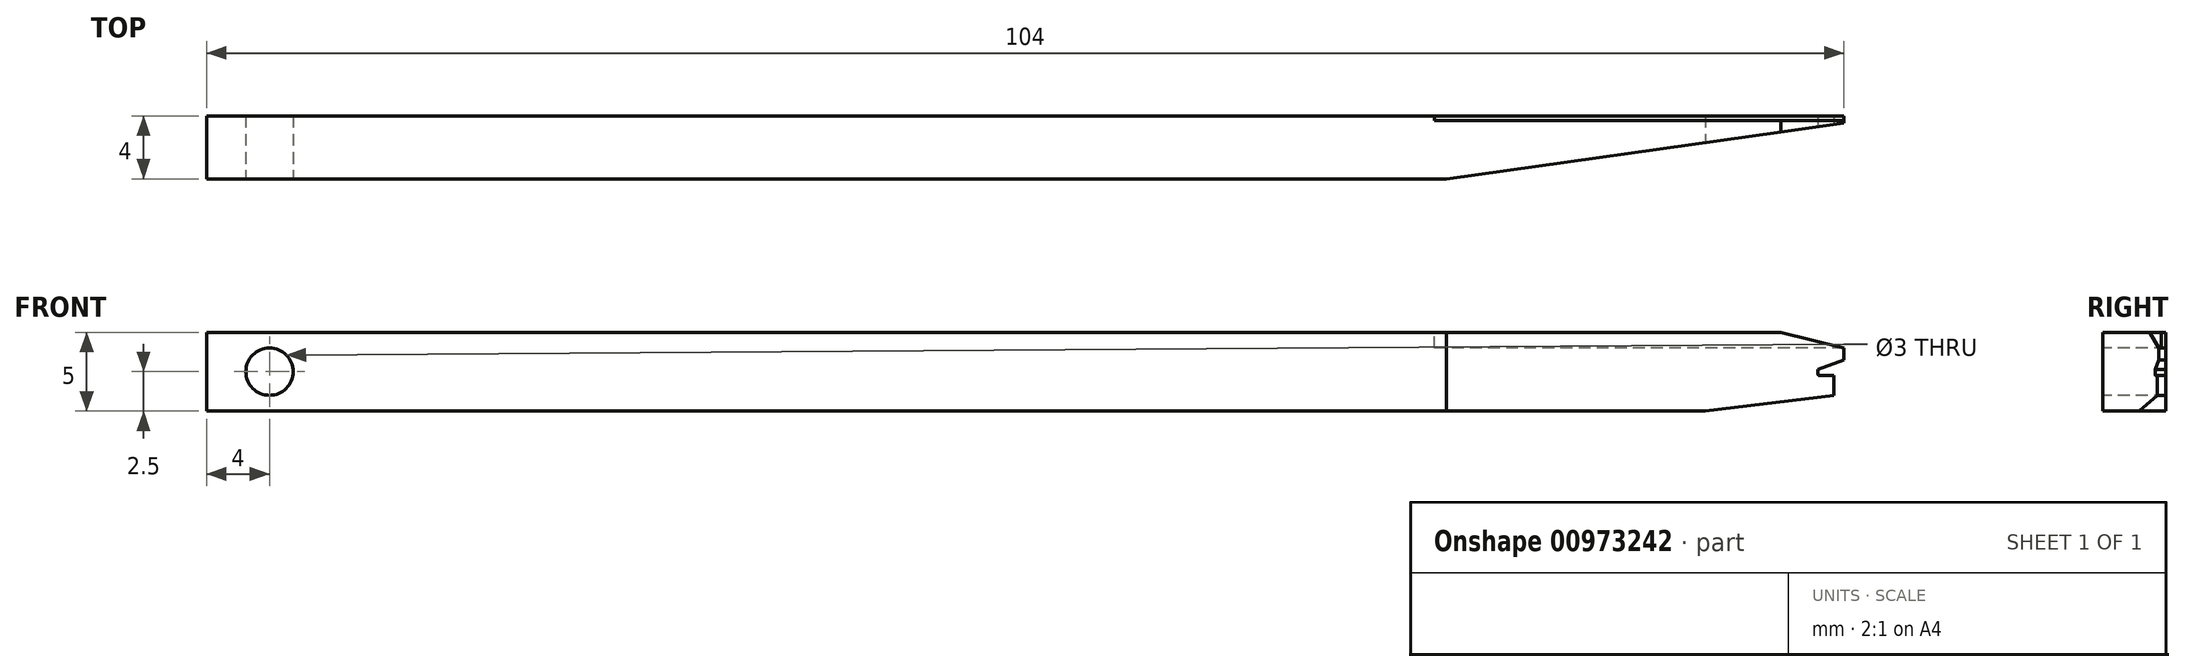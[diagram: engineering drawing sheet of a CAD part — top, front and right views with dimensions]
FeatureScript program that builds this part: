
annotation { "Feature Type Name" : "Feature", "Feature Type Description" : "" }
export const myFeature = defineFeature(function(context is Context, id is Id, definition is map)
    precondition{}
    {
        {
            var Q0;
            Q0=qCreatedBy(makeId("Front.planeOp"),FACE);
            var sketch = newSketch(context, id + "F0", { "sketchPlane" : qUnion([Q0])});
            skLineSegment(sketch, "E0.bottom", {"start": v(52, -2.5) * mm, "end": v(-52, -2.5) * mm});
            skLineSegment(sketch, "E0.top", {"start": v(52, 2.5) * mm, "end": v(-52, 2.5) * mm});
            skLineSegment(sketch, "E0.left", {"start": v(52, -2.5) * mm, "end": v(52, 2.5) * mm});
            skLineSegment(sketch, "E0.right", {"start": v(-52, -2.5) * mm, "end": v(-52, 2.5) * mm});
            skPoint(sketch, "E0.middle", {"position": v(0, 0) * mm});
            skSolve(sketch);
        }
        {
            var Q0;
            Q0 = qSketchRegion(id + "F0", true);
            extrude(context, id + "F1", {"entities" : qUnion([Q0]), "depth" : 4 * mm, "offsetDistance" : 25 * mm});
        }
        {
            var Q0;
            Q0=makeQuery(id+"F1.opExtrude","CAP_FACE",FACE,{"disambiguationData":[OSD([sQuery(id+"F0.wireOp",EDGE,"E0.bottom"),sQuery(id+"F0.wireOp",EDGE,"E0.top"),sQuery(id+"F0.wireOp",EDGE,"E0.left"),sQuery(id+"F0.wireOp",EDGE,"E0.right")])],"isStart":false});
            var sketch = newSketch(context, id + "F2", { "sketchPlane" : qUnion([Q0])});
            skLineSegment(sketch, "E1", {"start": v(-52, -2.5) * mm, "end": v(-48, -2.5) * mm});
            skLineSegment(sketch, "E2", {"start": v(-48, -2.5) * mm, "end": v(-48, 0) * mm});
            skCircle(sketch, "E3", {"center": v(-48, 0) * mm, "radius": 1.5 * mm});
            skSolve(sketch);
        }
        {
            var Q0;
            Q0 = qSketchRegion(id + "F2", true);
            extrude(context, id + "F3", {"entities" : qUnion([Q0]), "operationType" : NewBodyOperationType.REMOVE, "endBound" : BoundingType.UP_TO_NEXT, "oppositeDirection" : true, "depth" : 25 * mm, "offsetDistance" : 25 * mm});
        }
        {
            var Q0;
            Q0=makeQuery(id+"F1.opExtrude","CAP_FACE",FACE,{"disambiguationData":[OSD([sQuery(id+"F0.wireOp",EDGE,"E0.bottom"),sQuery(id+"F0.wireOp",EDGE,"E0.top"),sQuery(id+"F0.wireOp",EDGE,"E0.left"),sQuery(id+"F0.wireOp",EDGE,"E0.right")])],"isStart":false});
            var sketch = newSketch(context, id + "F4", { "sketchPlane" : qUnion([Q0])});
            skLineSegment(sketch, "E4.bottom", {"start": v(52, -2.5) * mm, "end": v(51.35, -2.5) * mm});
            skLineSegment(sketch, "E4.top", {"start": v(52, 0.75) * mm, "end": v(51.35, 0.75) * mm});
            skLineSegment(sketch, "E4.left", {"start": v(52, -2.5) * mm, "end": v(52, 0.75) * mm});
            skLineSegment(sketch, "E4.right", {"start": v(51.35, -2.5) * mm, "end": v(51.35, 0.75) * mm});
            skSolve(sketch);
        }
        {
            var Q0;
            Q0 = qSketchRegion(id + "F4", true);
            extrude(context, id + "F5", {"entities" : qUnion([Q0]), "operationType" : NewBodyOperationType.REMOVE, "endBound" : BoundingType.UP_TO_NEXT, "oppositeDirection" : true, "depth" : 25 * mm, "offsetDistance" : 25 * mm});
        }
        {
            var Q0;
            Q0=makeQuery(id+"F1.opExtrude","CAP_FACE",FACE,{"disambiguationData":[OSD([sQuery(id+"F0.wireOp",EDGE,"E0.bottom"),sQuery(id+"F0.wireOp",EDGE,"E0.top"),sQuery(id+"F0.wireOp",EDGE,"E0.left"),sQuery(id+"F0.wireOp",EDGE,"E0.right")])],"isStart":false});
            var sketch = newSketch(context, id + "F6", { "sketchPlane" : qUnion([Q0])});
            skLineSegment(sketch, "E5", {"start": v(51.35, -2.5) * mm, "end": v(51.35, -1.5) * mm});
            skLineSegment(sketch, "E6", {"start": v(51.35, -1.5) * mm, "end": v(43.2, -2.5) * mm});
            skLineSegment(sketch, "E7", {"start": v(43.2, -2.5) * mm, "end": v(51.35, -2.5) * mm});
            skSolve(sketch);
        }
        {
            var Q0;
            Q0 = qSketchRegion(id + "F6", true);
            extrude(context, id + "F7", {"entities" : qUnion([Q0]), "operationType" : NewBodyOperationType.REMOVE, "endBound" : BoundingType.UP_TO_NEXT, "oppositeDirection" : true, "depth" : 25 * mm, "offsetDistance" : 25 * mm});
        }
        {
            var Q0;
            Q0=makeQuery(id+"F1.opExtrude","CAP_FACE",FACE,{"disambiguationData":[OSD([sQuery(id+"F0.wireOp",EDGE,"E0.bottom"),sQuery(id+"F0.wireOp",EDGE,"E0.top"),sQuery(id+"F0.wireOp",EDGE,"E0.left"),sQuery(id+"F0.wireOp",EDGE,"E0.right")])],"isStart":false});
            var sketch = newSketch(context, id + "F8", { "sketchPlane" : qUnion([Q0])});
            skLineSegment(sketch, "E8.bottom", {"start": v(51.35, -0.25) * mm, "end": v(50.35, -0.25) * mm});
            skLineSegment(sketch, "E8.top", {"start": v(51.35, 0.15) * mm, "end": v(50.35, 0.15) * mm});
            skLineSegment(sketch, "E8.left", {"start": v(51.35, -0.25) * mm, "end": v(51.35, 0.15) * mm});
            skLineSegment(sketch, "E8.right", {"start": v(50.35, -0.25) * mm, "end": v(50.35, 0.15) * mm});
            skSolve(sketch);
        }
        {
            var Q0;
            Q0 = qSketchRegion(id + "F8", true);
            extrude(context, id + "F9", {"entities" : qUnion([Q0]), "operationType" : NewBodyOperationType.REMOVE, "endBound" : BoundingType.UP_TO_NEXT, "oppositeDirection" : true, "depth" : 25 * mm, "offsetDistance" : 25 * mm});
        }
        {
            var Q0;
            Q0=makeQuery(id+"F1.opExtrude","CAP_FACE",FACE,{"disambiguationData":[OSD([sQuery(id+"F0.wireOp",EDGE,"E0.bottom"),sQuery(id+"F0.wireOp",EDGE,"E0.top"),sQuery(id+"F0.wireOp",EDGE,"E0.left"),sQuery(id+"F0.wireOp",EDGE,"E0.right")])],"isStart":false});
            var sketch = newSketch(context, id + "F10", { "sketchPlane" : qUnion([Q0])});
            skLineSegment(sketch, "E9.bottom", {"start": v(51.35, 0.75) * mm, "end": v(52, 0.75) * mm});
            skLineSegment(sketch, "E9.top", {"start": v(51.35, 0.15) * mm, "end": v(52, 0.15) * mm});
            skLineSegment(sketch, "E9.left", {"start": v(51.35, 0.75) * mm, "end": v(51.35, 0.15) * mm});
            skLineSegment(sketch, "E9.right", {"start": v(52, 0.75) * mm, "end": v(52, 0.15) * mm});
            skSolve(sketch);
        }
        {
            var Q0;
            Q0 = qSketchRegion(id + "F10", true);
            extrude(context, id + "F11", {"entities" : qUnion([Q0]), "operationType" : NewBodyOperationType.ADD, "oppositeDirection" : true, "depth" : 4 * mm, "offsetDistance" : 25 * mm});
        }
        {
            var Q0;
            Q0=makeQuery(id+"F11.boolean.opBoolean","MERGE",FACE,{"derivedFrom":[makeQuery(id+"F1.opExtrude","CAP_FACE",FACE,{"disambiguationData":[OSD([sQuery(id+"F0.wireOp",EDGE,"E0.bottom"),sQuery(id+"F0.wireOp",EDGE,"E0.top"),sQuery(id+"F0.wireOp",EDGE,"E0.left"),sQuery(id+"F0.wireOp",EDGE,"E0.right")])],"isStart":false}),makeQuery(id+"F11.opExtrude","CAP_FACE",FACE,{"disambiguationData":[OSD([sQuery(id+"F10.wireOp",EDGE,"E9.bottom"),sQuery(id+"F10.wireOp",EDGE,"E9.top"),sQuery(id+"F10.wireOp",EDGE,"E9.left"),sQuery(id+"F10.wireOp",EDGE,"E9.right")])],"isStart":true})]});
            var sketch = newSketch(context, id + "F12", { "sketchPlane" : qUnion([Q0])});
            skLineSegment(sketch, "E10", {"start": v(52, 0.75) * mm, "end": v(50.35, 0.15) * mm});
            skLineSegment(sketch, "E11", {"start": v(50.35, 0.15) * mm, "end": v(52, 0.15) * mm});
            skLineSegment(sketch, "E12", {"start": v(52, 0.15) * mm, "end": v(52, 0.75) * mm});
            skSolve(sketch);
        }
        {
            var Q0;
            Q0 = qSketchRegion(id + "F12", true);
            extrude(context, id + "F13", {"entities" : qUnion([Q0]), "operationType" : NewBodyOperationType.REMOVE, "endBound" : BoundingType.UP_TO_NEXT, "oppositeDirection" : true, "depth" : 25 * mm, "offsetDistance" : 25 * mm});
        }
        {
            var Q0;
            Q0=makeQuery(id+"F11.boolean.opBoolean","MERGE",FACE,{"derivedFrom":[makeQuery(id+"F1.opExtrude","CAP_FACE",FACE,{"disambiguationData":[OSD([sQuery(id+"F0.wireOp",EDGE,"E0.bottom"),sQuery(id+"F0.wireOp",EDGE,"E0.top"),sQuery(id+"F0.wireOp",EDGE,"E0.left"),sQuery(id+"F0.wireOp",EDGE,"E0.right")])],"isStart":false}),makeQuery(id+"F11.opExtrude","CAP_FACE",FACE,{"disambiguationData":[OSD([sQuery(id+"F10.wireOp",EDGE,"E9.bottom"),sQuery(id+"F10.wireOp",EDGE,"E9.top"),sQuery(id+"F10.wireOp",EDGE,"E9.left"),sQuery(id+"F10.wireOp",EDGE,"E9.right")])],"isStart":true})]});
            var sketch = newSketch(context, id + "F14", { "sketchPlane" : qUnion([Q0])});
            skLineSegment(sketch, "E13", {"start": v(52, 2.5) * mm, "end": v(52, 1.5) * mm});
            skLineSegment(sketch, "E14", {"start": v(52, 2.5) * mm, "end": v(48, 2.5) * mm});
            skLineSegment(sketch, "E15", {"start": v(48, 2.5) * mm, "end": v(52, 1.5) * mm});
            skSolve(sketch);
        }
        {
            var Q0;
            Q0 = qSketchRegion(id + "F14", true);
            extrude(context, id + "F15", {"entities" : qUnion([Q0]), "operationType" : NewBodyOperationType.REMOVE, "endBound" : BoundingType.UP_TO_NEXT, "oppositeDirection" : true, "depth" : 25 * mm, "offsetDistance" : 25 * mm});
        }
        {
            var Q0;
            Q0=makeQuery(id+"F1.opExtrude","SWEPT_FACE",FACE,{"disambiguationData":[OSD([sQuery(id+"F0.wireOp",EDGE,"E0.top")])]});
            var sketch = newSketch(context, id + "F16", { "sketchPlane" : qUnion([Q0])});
            skLineSegment(sketch, "E16", {"start": v(52, -0.45) * mm, "end": v(26.74, -4) * mm});
            skLineSegment(sketch, "E17", {"start": v(26.74, -4) * mm, "end": v(52, -4) * mm});
            skLineSegment(sketch, "E18", {"start": v(52, -4) * mm, "end": v(52, -0.45) * mm});
            skSolve(sketch);
        }
        {
            var Q0;
            Q0 = qSketchRegion(id + "F16", true);
            extrude(context, id + "F17", {"entities" : qUnion([Q0]), "operationType" : NewBodyOperationType.REMOVE, "endBound" : BoundingType.UP_TO_NEXT, "oppositeDirection" : true, "depth" : 25 * mm, "offsetDistance" : 25 * mm});
        }
        {
            var Q0;
            Q0=makeQuery(id+"F9.boolean.opBoolean","COPY",EDGE,{"derivedFrom":makeQuery(id+"F9.opExtrude","SWEPT_EDGE",EDGE,{"disambiguationData":[OSD([sQuery(id+"F8.wireOp",EDGE,"E8.bottom"),sQuery(id+"F8.wireOp",EDGE,"E8.right")])]})});
            fillet(context, id + "F18", {"entities" : qUnion([Q0]), "radius" : 0.1 * mm, "tangentPropagation" : true, "allowEdgeOverflow" : false});
        }
        {
            var Q0;
            Q0=makeQuery(id+"F11.boolean.opBoolean","MERGE",FACE,{"derivedFrom":[makeQuery(id+"F1.opExtrude","CAP_FACE",FACE,{"disambiguationData":[OSD([sQuery(id+"F0.wireOp",EDGE,"E0.bottom"),sQuery(id+"F0.wireOp",EDGE,"E0.top"),sQuery(id+"F0.wireOp",EDGE,"E0.left"),sQuery(id+"F0.wireOp",EDGE,"E0.right")])],"isStart":true}),makeQuery(id+"F11.opExtrude","CAP_FACE",FACE,{"disambiguationData":[OSD([sQuery(id+"F10.wireOp",EDGE,"E9.bottom"),sQuery(id+"F10.wireOp",EDGE,"E9.top"),sQuery(id+"F10.wireOp",EDGE,"E9.left"),sQuery(id+"F10.wireOp",EDGE,"E9.right")])],"isStart":false})]});
            var sketch = newSketch(context, id + "F19", { "sketchPlane" : qUnion([Q0])});
            skLineSegment(sketch, "E19", {"start": v(-52, 1.5) * mm, "end": v(-26, 1.5) * mm});
            skLineSegment(sketch, "E20", {"start": v(-26, 1.5) * mm, "end": v(-26, 2.5) * mm});
            skLineSegment(sketch, "E21", {"start": v(-26, 2.5) * mm, "end": v(-48, 2.5) * mm});
            skLineSegment(sketch, "E22", {"start": v(-48, 2.5) * mm, "end": v(-52, 1.5) * mm});
            skSolve(sketch);
        }
        {
            var Q0;
            Q0 = qSketchRegion(id + "F19", true);
            extrude(context, id + "F20", {"entities" : qUnion([Q0]), "operationType" : NewBodyOperationType.REMOVE, "oppositeDirection" : true, "depth" : 0.3 * mm, "offsetDistance" : 25 * mm});
        }
    });
